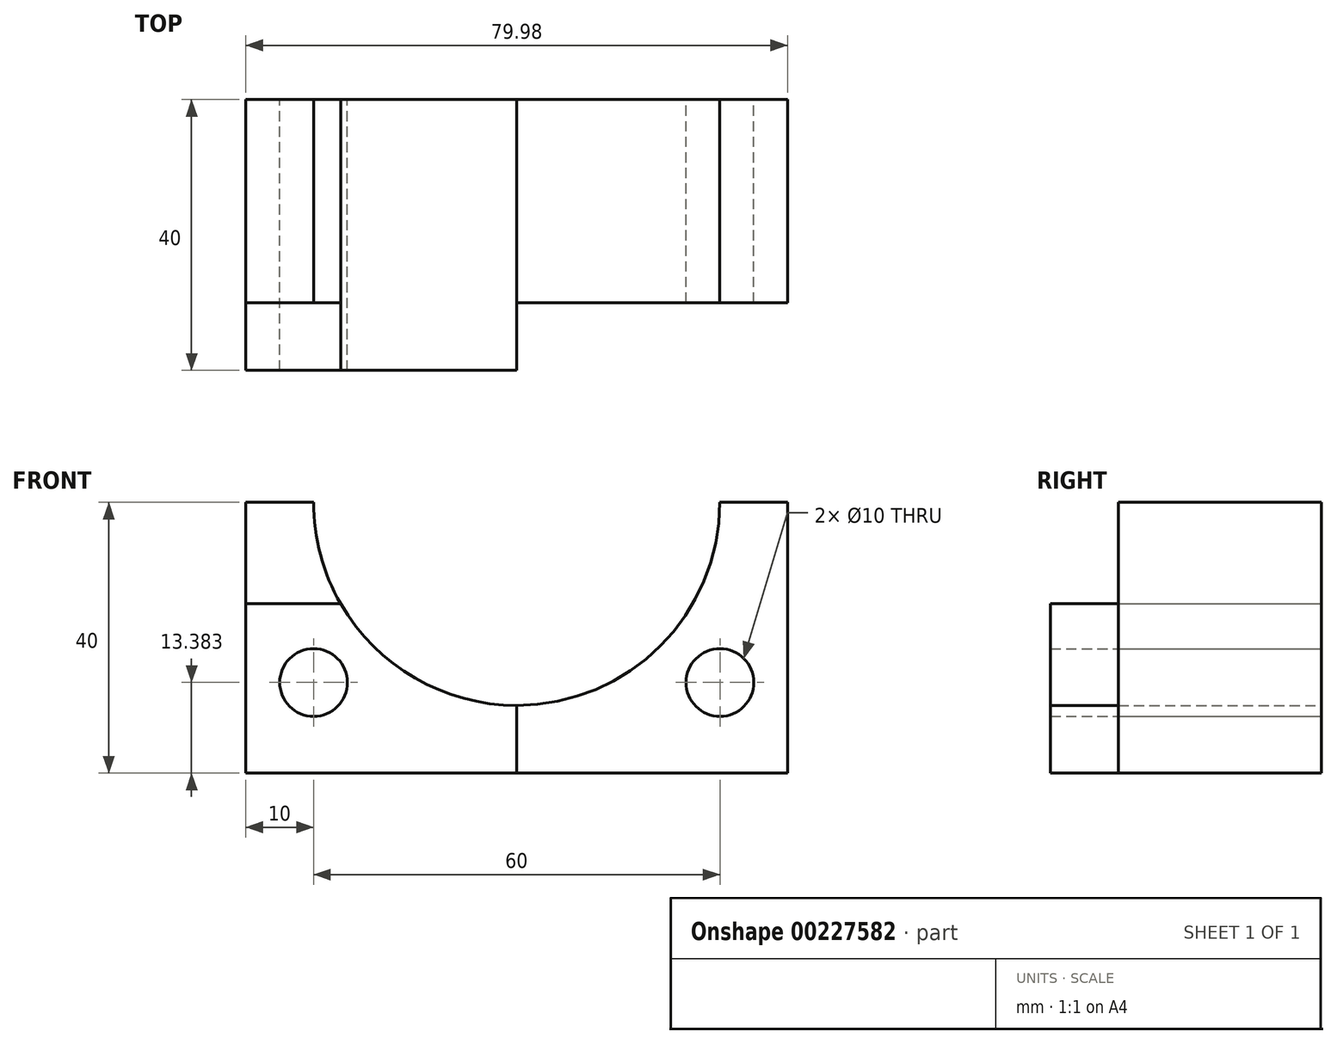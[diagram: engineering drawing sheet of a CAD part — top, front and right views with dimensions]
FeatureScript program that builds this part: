
annotation { "Feature Type Name" : "Feature", "Feature Type Description" : "" }
export const myFeature = defineFeature(function(context is Context, id is Id, definition is map)
    precondition{}
    {
        {
            var Q0;
            Q0=qCreatedBy(makeId("Front.planeOp"),FACE);
            var sketch = newSketch(context, id + "F0", { "sketchPlane" : qUnion([Q0])});
            skLineSegment(sketch, "E0", {"start": v(-40, 20) * mm, "end": v(-40, -20) * mm});
            skLineSegment(sketch, "E1", {"start": v(-40, -20) * mm, "end": v(40, -20) * mm});
            skLineSegment(sketch, "E2", {"start": v(39.98, -20) * mm, "end": v(39.98, 20) * mm});
            skLineSegment(sketch, "E3", {"start": v(39.98, 20) * mm, "end": v(29.99, 20) * mm});
            skPoint(sketch, "E4", {"position": v(0, -20) * mm});
            skPoint(sketch, "E5", {"position": v(39.98, 0) * mm});
            skArc(sketch, "E6", {"start": v(-30.01, 20) * mm, "mid": v(-0.01, -10) * mm, "end": v(29.99, 20) * mm});
            skLineSegment(sketch, "E7", {"start": v(-40, 5) * mm, "end": v(-26, 5) * mm});
            skLineSegment(sketch, "E8.trimOffspring", {"start": v(-30.01, 20) * mm, "end": v(-40, 20) * mm});
            skCircle(sketch, "E9", {"center": v(-30, -6.62) * mm, "radius": 5 * mm});
            skCircle(sketch, "E10", {"center": v(30, -6.62) * mm, "radius": 5 * mm});
            skLineSegment(sketch, "E11", {"start": v(-0.01, -10) * mm, "end": v(0, -20) * mm});
            skSolve(sketch);
        }
        {
            var Q0;
            {var subQ1=sQuery(id+"F0.wireOp",EDGE,"E2");Q0=makeQuery(id+"F0.imprint","IMPRINT",FACE,{"disambiguationData":[TD([[makeQuery(id+"F0.imprint","IMPRINT",EDGE,{"derivedFrom":subQ1}),1.0]])]});}
            extrude(context, id + "F1", {"entities" : qUnion([Q0]), "depth" : 25 * mm});
        }
        {
            var Q0;
            {var subQ3=sQuery(id+"F0.wireOp",EDGE,"E2");Q0=makeQuery(id+"F0.imprint","IMPRINT",FACE,{"disambiguationData":[TD([[makeQuery(id+"F0.imprint","IMPRINT",EDGE,{"derivedFrom":subQ3}),1.0]])]});}
            var Q1;
            {var subQ2=sQuery(id+"F0.wireOp",EDGE,"E7");Q1=makeQuery(id+"F0.imprint","IMPRINT",FACE,{"disambiguationData":[TD([[makeQuery(id+"F0.imprint","IMPRINT",EDGE,{"derivedFrom":subQ2}),1.0]])]});}
            extrude(context, id + "F2", {"entities" : qUnion([Q0, Q1]), "operationType" : NewBodyOperationType.ADD, "depth" : 30 * mm});
        }
        {
            var Q0;
            {var subQ0=sQuery(id+"F0.wireOp",EDGE,"E7");Q0=makeQuery(id+"F0.imprint","IMPRINT",FACE,{"disambiguationData":[TD([[makeQuery(id+"F0.imprint","IMPRINT",EDGE,{"derivedFrom":subQ0}),-1.0]])]});}
            extrude(context, id + "F3", {"entities" : qUnion([Q0]), "depth" : 40 * mm});
        }
    });
